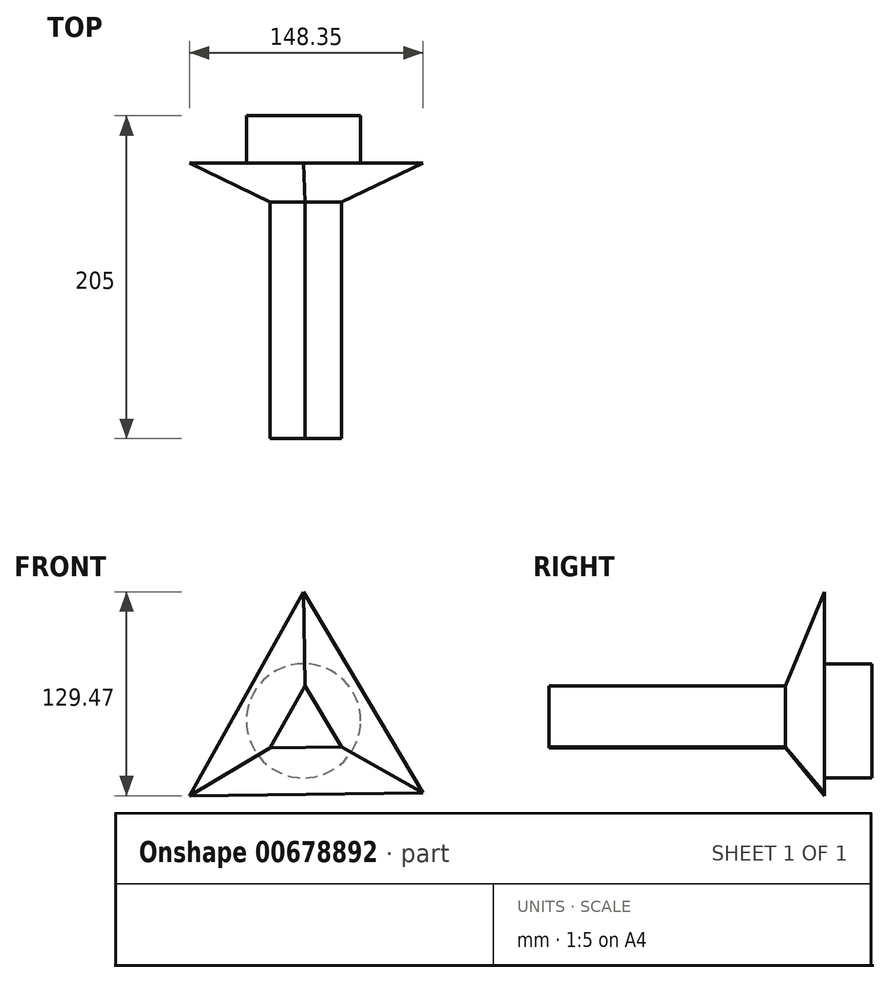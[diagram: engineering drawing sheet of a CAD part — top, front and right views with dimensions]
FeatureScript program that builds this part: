
annotation { "Feature Type Name" : "Feature", "Feature Type Description" : "" }
export const myFeature = defineFeature(function(context is Context, id is Id, definition is map)
    precondition{}
    {
        {
            var Q0;
            Q0=qCreatedBy(makeId("Front.planeOp"),FACE);
            var sketch = newSketch(context, id + "F0", { "sketchPlane" : qUnion([Q0])});
            skLineSegment(sketch, "E0.0", {"start": v(28.6, -16.54) * mm, "end": v(-16.56, -17.14) * mm});
            skLineSegment(sketch, "E0.1", {"start": v(-16.56, -17.14) * mm, "end": v(5.5, 22.27) * mm});
            skLineSegment(sketch, "E0.2", {"start": v(5.5, 22.27) * mm, "end": v(28.6, -16.54) * mm});
            skSolve(sketch);
        }
        {
            var Q0;
            Q0 = qSketchRegion(id + "F0", true);
            extrude(context, id + "F1", {"entities" : qUnion([Q0]), "depth" : 150 * mm, "offsetDistance" : 25 * mm});
        }
        {
            var Q0;
            Q0=makeQuery(id+"F1.opExtrude","CAP_FACE",FACE,{"disambiguationData":[OSD([sQuery(id+"F0.wireOp",EDGE,"E0.0"),sQuery(id+"F0.wireOp",EDGE,"E0.1"),sQuery(id+"F0.wireOp",EDGE,"E0.2")])],"isStart":true});
            extrude(context, id + "F2", {"entities" : qUnion([Q0]), "operationType" : NewBodyOperationType.ADD, "depth" : 25 * mm, "offsetDistance" : 25 * mm, "hasDraft" : true, "draftAngle" : 50 * degree});
        }
        {
            var Q0;
            Q0=makeQuery(id+"F2.opExtrude","CAP_FACE",FACE,{"disambiguationData":[OSD([sQuery(id+"F0.wireOp",EDGE,"E0.0"),sQuery(id+"F0.wireOp",EDGE,"E0.1"),sQuery(id+"F0.wireOp",EDGE,"E0.2")])],"isStart":false});
            var sketch = newSketch(context, id + "F3", { "sketchPlane" : qUnion([Q0])});
            skCircle(sketch, "E1", {"center": v(-4.63, 0) * mm, "radius": 36.28 * mm});
            skSolve(sketch);
        }
        {
            var Q0;
            Q0 = qSketchRegion(id + "F3", true);
            extrude(context, id + "F4", {"entities" : qUnion([Q0]), "operationType" : NewBodyOperationType.ADD, "depth" : 30 * mm, "offsetDistance" : 25 * mm});
        }
    });
